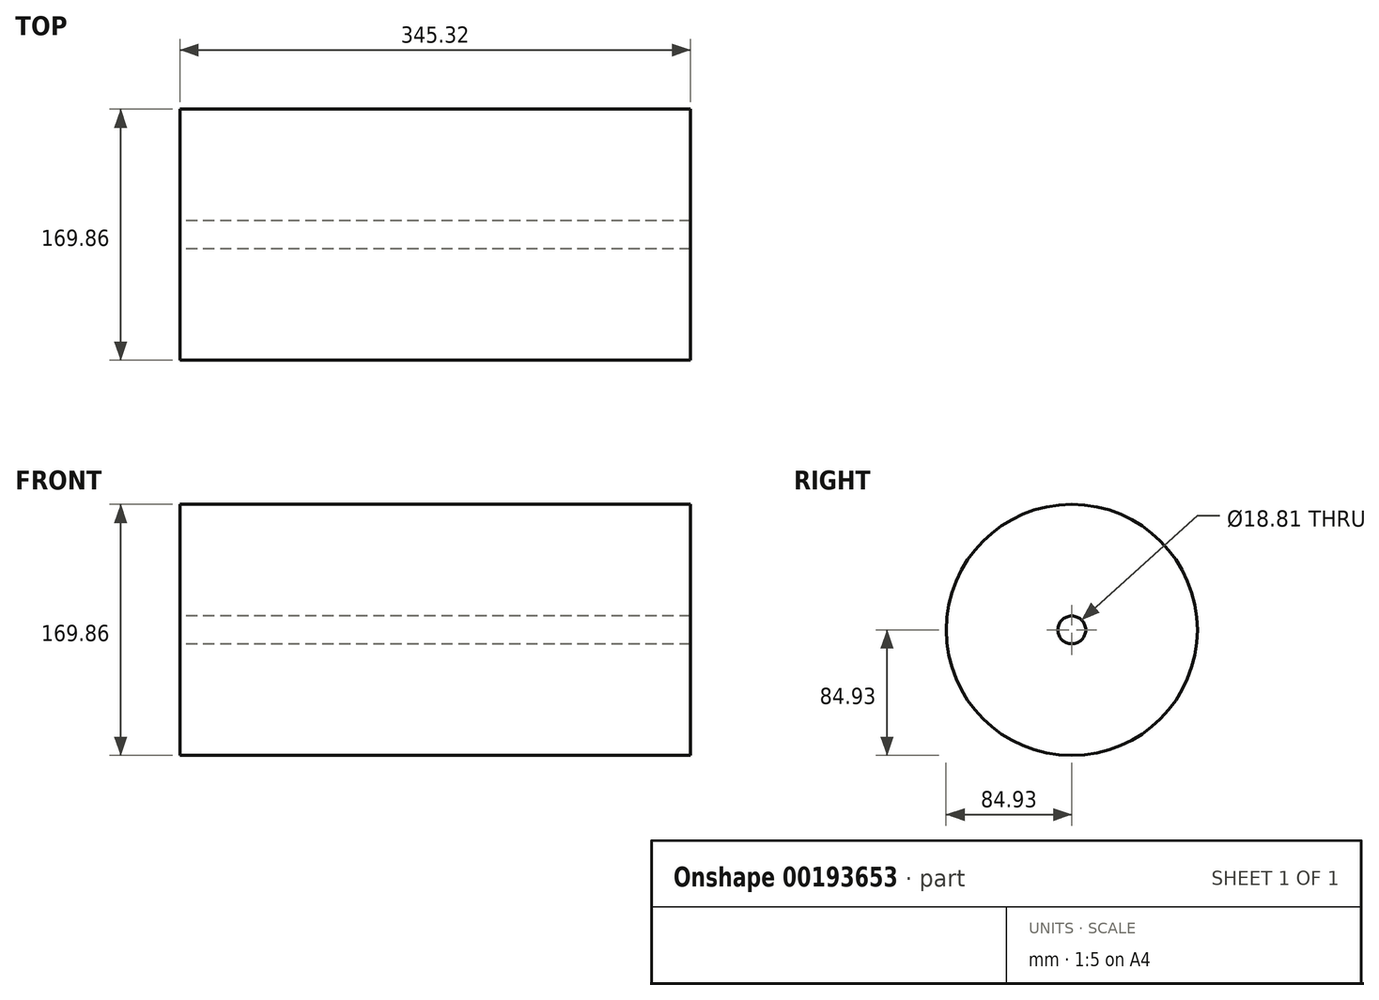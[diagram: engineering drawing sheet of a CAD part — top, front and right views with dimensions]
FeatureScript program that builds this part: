
annotation { "Feature Type Name" : "Feature", "Feature Type Description" : "" }
export const myFeature = defineFeature(function(context is Context, id is Id, definition is map)
    precondition{}
    {
        {
            var Q0;
            Q0=qCreatedBy(makeId("Top.planeOp"),FACE);
            var sketch = newSketch(context, id + "F0", { "sketchPlane" : qUnion([Q0])});
            skLineSegment(sketch, "E0", {"start": v(0, 0) * mm, "end": v(135.88, 0) * mm});
            skLineSegment(sketch, "E1", {"start": v(0, 0) * mm, "end": v(-209.44, 0) * mm});
            skLineSegment(sketch, "E2.bottom", {"start": v(-209.44, 84.93) * mm, "end": v(135.88, 84.93) * mm});
            skLineSegment(sketch, "E2.top", {"start": v(-209.44, 9.4) * mm, "end": v(135.88, 9.4) * mm});
            skLineSegment(sketch, "E2.left", {"start": v(-209.44, 84.93) * mm, "end": v(-209.44, 9.4) * mm});
            skLineSegment(sketch, "E2.right", {"start": v(135.88, 84.93) * mm, "end": v(135.88, 9.4) * mm});
            skSolve(sketch);
        }
        {
            var Q0;
            Q0=makeQuery(id+"F0.imprint","IMPRINT",FACE,{"disambiguationData":[TD([[makeQuery(id+"F0.imprint","IMPRINT",EDGE,{"derivedFrom":sQuery(id+"F0.wireOp",EDGE,"E2.bottom")}),-1.0]])]});
            var Q1;
            Q1=sQuery(id+"F0.wireOp",EDGE,"E0");
            revolve(context, id + "F1", {"entities" : qUnion([Q0]), "axis" : qUnion([Q1]), "revolveType" : RevolveType.FULL});
        }
    });
